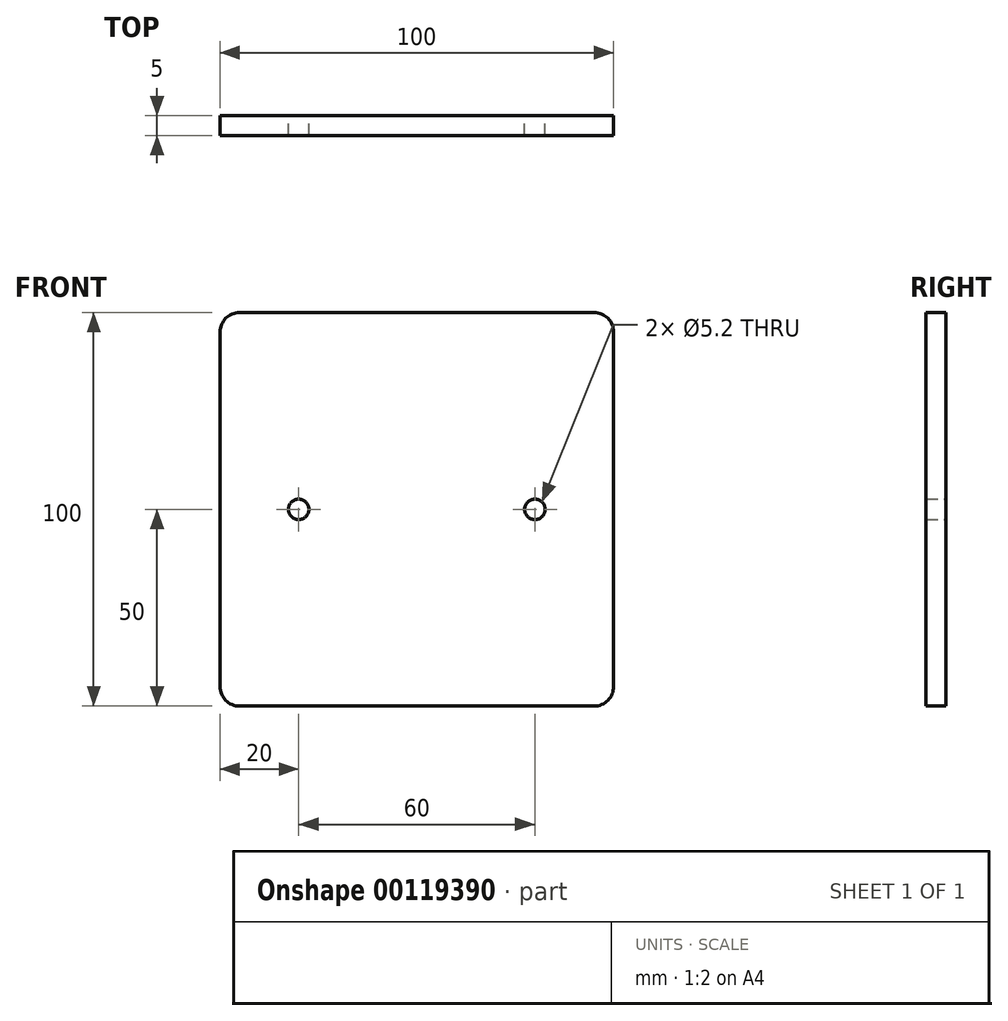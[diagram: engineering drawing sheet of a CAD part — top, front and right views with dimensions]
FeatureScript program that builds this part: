
annotation { "Feature Type Name" : "Feature", "Feature Type Description" : "" }
export const myFeature = defineFeature(function(context is Context, id is Id, definition is map)
    precondition{}
    {
        {
            var Q0;
            Q0=qCreatedBy(makeId("Front.planeOp"),FACE);
            var sketch = newSketch(context, id + "F0", { "sketchPlane" : qUnion([Q0])});
            skLineSegment(sketch, "E0.bottom", {"start": v(45, -50) * mm, "end": v(-45, -50) * mm});
            skLineSegment(sketch, "E0.top", {"start": v(45, 50) * mm, "end": v(-45, 50) * mm});
            skLineSegment(sketch, "E0.left", {"start": v(50, -45) * mm, "end": v(50, 45) * mm});
            skLineSegment(sketch, "E0.right", {"start": v(-50, -45) * mm, "end": v(-50, 45) * mm});
            skPoint(sketch, "E0.middle", {"position": v(0, 0) * mm});
            skLineSegment(sketch, "E1", {"start": v(-50, 0) * mm, "end": v(50, 0) * mm, "construction": true});
            skCircle(sketch, "E2", {"center": v(-30, 0) * mm, "radius": 2.6 * mm});
            skCircle(sketch, "E3", {"center": v(30, 0) * mm, "radius": 2.6 * mm});
            skPoint(sketch, "E4.visualSharp", {"position": v(-50, 50) * mm});
            skArc(sketch, "E4.filletArc", {"start": v(-45, 50) * mm, "mid": v(-48.54, 48.54) * mm, "end": v(-50, 45) * mm});
            skPoint(sketch, "E5.visualSharp", {"position": v(-50, -50) * mm});
            skArc(sketch, "E5.filletArc", {"start": v(-50, -45) * mm, "mid": v(-48.54, -48.54) * mm, "end": v(-45, -50) * mm});
            skPoint(sketch, "E6.visualSharp", {"position": v(50, -50) * mm});
            skArc(sketch, "E6.filletArc", {"start": v(45, -50) * mm, "mid": v(48.54, -48.54) * mm, "end": v(50, -45) * mm});
            skPoint(sketch, "E7.visualSharp", {"position": v(50, 50) * mm});
            skArc(sketch, "E7.filletArc", {"start": v(50, 45) * mm, "mid": v(48.54, 48.54) * mm, "end": v(45, 50) * mm});
            skSolve(sketch);
        }
        {
            var Q0;
            Q0=makeQuery(id+"F0.imprint","IMPRINT",FACE,{"disambiguationData":[TD([[makeQuery(id+"F0.imprint","IMPRINT",EDGE,{"derivedFrom":sQuery(id+"F0.wireOp",EDGE,"E0.bottom")}),-1.0]])]});
            extrude(context, id + "F1", {"entities" : qUnion([Q0]), "depth" : 5 * mm});
        }
    });
